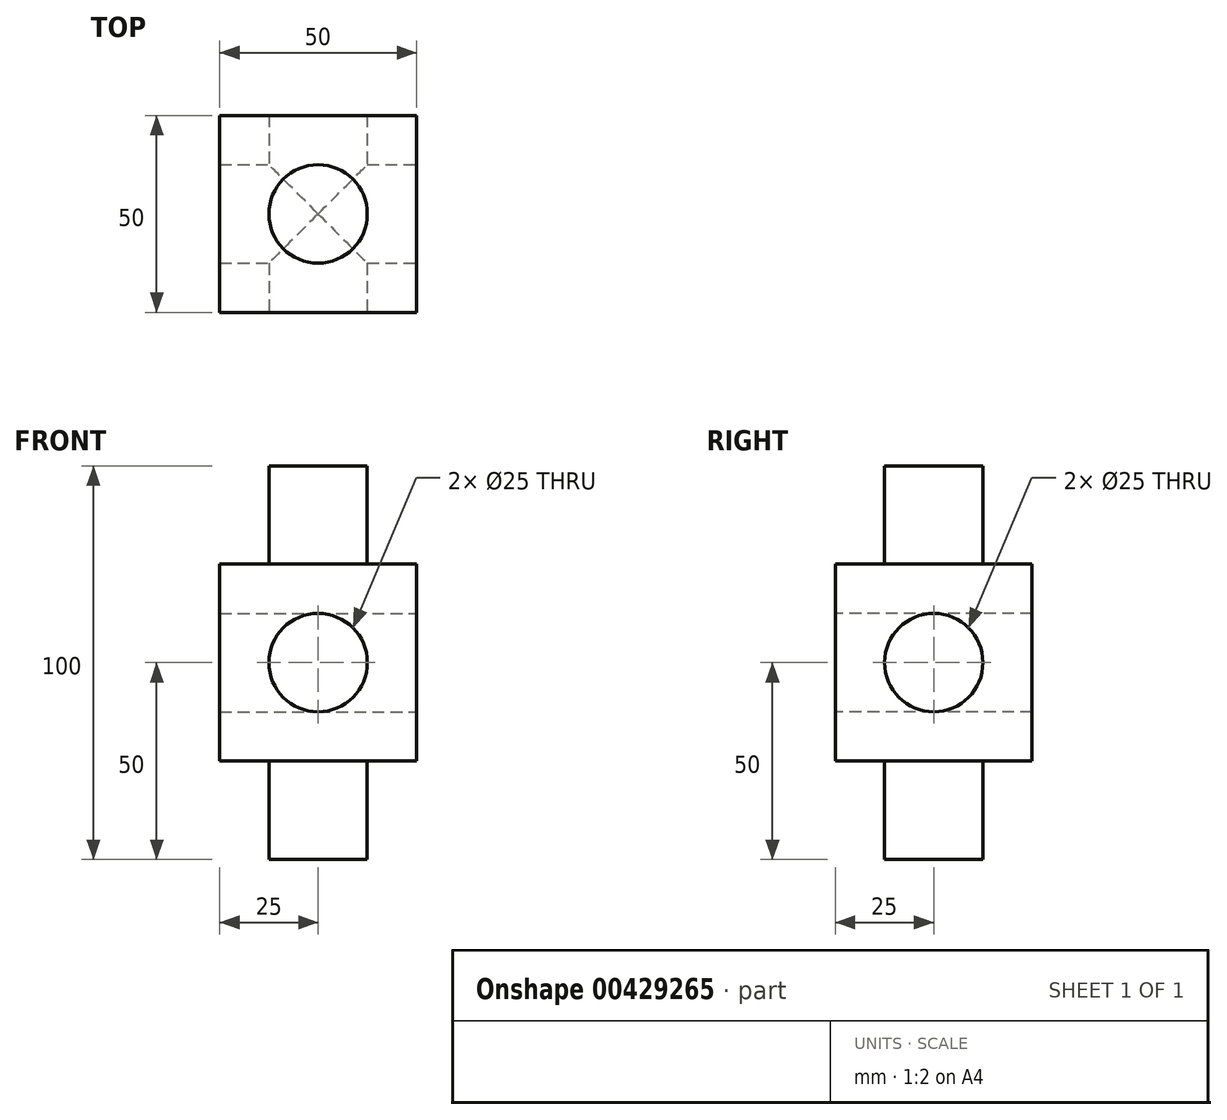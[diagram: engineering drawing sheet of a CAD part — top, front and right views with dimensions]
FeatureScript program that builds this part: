
annotation { "Feature Type Name" : "Feature", "Feature Type Description" : "" }
export const myFeature = defineFeature(function(context is Context, id is Id, definition is map)
    precondition{}
    {
        {
            var Q0;
            Q0=qCreatedBy(makeId("Front.planeOp"),FACE);
            var sketch = newSketch(context, id + "F0", { "sketchPlane" : qUnion([Q0])});
            skLineSegment(sketch, "E0.bottom", {"start": v(0, 0) * mm, "end": v(50, 0) * mm});
            skLineSegment(sketch, "E0.top", {"start": v(0, 50) * mm, "end": v(50, 50) * mm});
            skLineSegment(sketch, "E0.left", {"start": v(0, 0) * mm, "end": v(0, 50) * mm});
            skLineSegment(sketch, "E0.right", {"start": v(50, 0) * mm, "end": v(50, 50) * mm});
            skSolve(sketch);
        }
        {
            var Q0;
            Q0 = qSketchRegion(id + "F0", true);
            extrude(context, id + "F1", {"entities" : qUnion([Q0]), "depth" : 50 * mm});
        }
        {
            var Q0;
            Q0=makeQuery(id+"F1.opExtrude","SWEPT_FACE",FACE,{"disambiguationData":[OSD([sQuery(id+"F0.wireOp",EDGE,"E0.top")])]});
            var sketch = newSketch(context, id + "F2", { "sketchPlane" : qUnion([Q0])});
            skCircle(sketch, "E1", {"center": v(25, -25) * mm, "radius": 12.5 * mm});
            skPoint(sketch, "E1.centerSnap0", {"position": v(0, -25) * mm});
            skPoint(sketch, "E1.centerSnap1", {"position": v(25, 0) * mm});
            skSolve(sketch);
        }
        {
            var Q0;
            Q0 = qSketchRegion(id + "F2", true);
            extrude(context, id + "F3", {"entities" : qUnion([Q0]), "operationType" : NewBodyOperationType.ADD, "depth" : 25 * mm});
        }
        {
            var Q0;
            Q0=makeQuery(id+"F1.opExtrude","SWEPT_FACE",FACE,{"disambiguationData":[OSD([sQuery(id+"F0.wireOp",EDGE,"E0.right")])]});
            var sketch = newSketch(context, id + "F4", { "sketchPlane" : qUnion([Q0])});
            skCircle(sketch, "E2", {"center": v(-25, 25) * mm, "radius": 12.5 * mm});
            skPoint(sketch, "E2.centerSnap0", {"position": v(-50, 25) * mm});
            skPoint(sketch, "E2.centerSnap1", {"position": v(-25, 50) * mm});
            skSolve(sketch);
        }
        {
            var Q0;
            Q0 = qSketchRegion(id + "F4", true);
            extrude(context, id + "F5", {"entities" : qUnion([Q0]), "operationType" : NewBodyOperationType.REMOVE, "oppositeDirection" : true, "depth" : 50 * mm});
        }
        {
            var Q0;
            Q0=makeQuery(id+"F1.opExtrude","CAP_FACE",FACE,{"disambiguationData":[OSD([sQuery(id+"F0.wireOp",EDGE,"E0.bottom"),sQuery(id+"F0.wireOp",EDGE,"E0.top"),sQuery(id+"F0.wireOp",EDGE,"E0.left"),sQuery(id+"F0.wireOp",EDGE,"E0.right")])],"isStart":false});
            var sketch = newSketch(context, id + "F6", { "sketchPlane" : qUnion([Q0])});
            skCircle(sketch, "E3", {"center": v(25, 25) * mm, "radius": 12.5 * mm});
            skPoint(sketch, "E3.centerSnap0", {"position": v(0, 25) * mm});
            skPoint(sketch, "E3.centerSnap1", {"position": v(25, 50) * mm});
            skSolve(sketch);
        }
        {
            var Q0;
            Q0 = qSketchRegion(id + "F6", true);
            extrude(context, id + "F7", {"entities" : qUnion([Q0]), "operationType" : NewBodyOperationType.REMOVE, "oppositeDirection" : true, "depth" : 50 * mm});
        }
        {
            var Q0;
            Q0=makeQuery(id+"F1.opExtrude","SWEPT_FACE",FACE,{"disambiguationData":[OSD([sQuery(id+"F0.wireOp",EDGE,"E0.bottom")])]});
            var sketch = newSketch(context, id + "F8", { "sketchPlane" : qUnion([Q0])});
            skCircle(sketch, "E4", {"center": v(25, 25) * mm, "radius": 12.5 * mm});
            skPoint(sketch, "E4.centerSnap0", {"position": v(0, 25) * mm});
            skPoint(sketch, "E4.centerSnap1", {"position": v(25, 50) * mm});
            skSolve(sketch);
        }
        {
            var Q0;
            Q0 = qSketchRegion(id + "F8", true);
            extrude(context, id + "F9", {"entities" : qUnion([Q0]), "operationType" : NewBodyOperationType.ADD, "depth" : 25 * mm});
        }
    });
